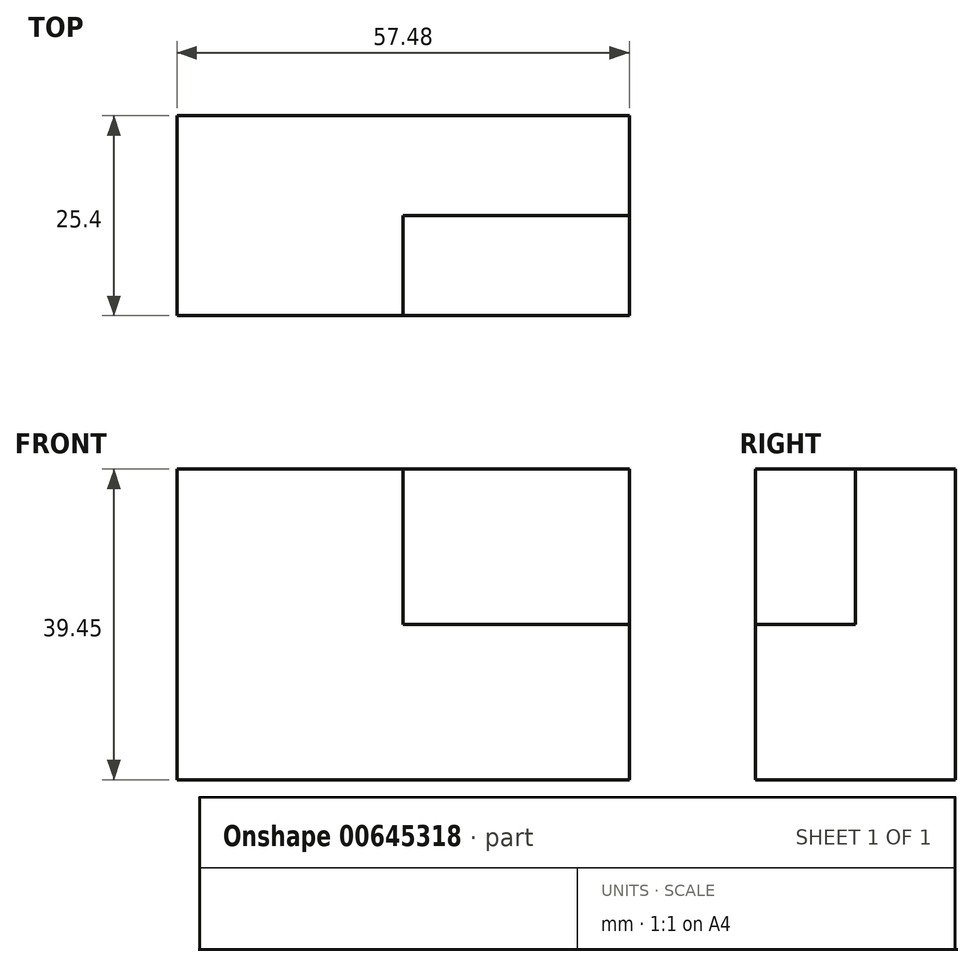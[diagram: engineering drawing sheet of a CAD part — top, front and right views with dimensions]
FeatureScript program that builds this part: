
annotation { "Feature Type Name" : "Feature", "Feature Type Description" : "" }
export const myFeature = defineFeature(function(context is Context, id is Id, definition is map)
    precondition{}
    {
        {
            var Q0;
            Q0=qCreatedBy(makeId("Front.planeOp"),FACE);
            var sketch = newSketch(context, id + "F0", { "sketchPlane" : qUnion([Q0])});
            skLineSegment(sketch, "E0.bottom", {"start": v(0, 0) * mm, "end": v(57.48, 0) * mm});
            skLineSegment(sketch, "E0.top", {"start": v(0, 39.45) * mm, "end": v(57.48, 39.45) * mm});
            skLineSegment(sketch, "E0.left", {"start": v(0, 0) * mm, "end": v(0, 39.45) * mm});
            skLineSegment(sketch, "E0.right", {"start": v(57.48, 0) * mm, "end": v(57.48, 39.45) * mm});
            skSolve(sketch);
        }
        {
            var Q0;
            Q0 = qSketchRegion(id + "F0", true);
            extrude(context, id + "F1", {"entities" : qUnion([Q0]), "depth" : 25.4 * mm, "offsetDistance" : 25.4 * mm});
        }
        {
            var Q0;
            Q0=makeQuery(id+"F1.opExtrude","CAP_FACE",FACE,{"disambiguationData":[OSD([sQuery(id+"F0.wireOp",EDGE,"E0.bottom"),sQuery(id+"F0.wireOp",EDGE,"E0.top"),sQuery(id+"F0.wireOp",EDGE,"E0.left"),sQuery(id+"F0.wireOp",EDGE,"E0.right")])],"isStart":false});
            var sketch = newSketch(context, id + "F2", { "sketchPlane" : qUnion([Q0])});
            skPoint(sketch, "E1.oppositeSnap0", {"position": v(57.48, 19.73) * mm});
            skPoint(sketch, "E1.oppositeSnap1", {"position": v(28.74, 39.45) * mm});
            skLineSegment(sketch, "E1.bottom", {"start": v(57.48, 39.45) * mm, "end": v(28.74, 39.45) * mm});
            skLineSegment(sketch, "E1.top", {"start": v(57.48, 19.73) * mm, "end": v(28.74, 19.73) * mm});
            skLineSegment(sketch, "E1.left", {"start": v(57.48, 39.45) * mm, "end": v(57.48, 19.73) * mm});
            skLineSegment(sketch, "E1.right", {"start": v(28.74, 39.45) * mm, "end": v(28.74, 19.73) * mm});
            skSolve(sketch);
        }
        {
            var Q0;
            Q0 = qSketchRegion(id + "F2", true);
            extrude(context, id + "F3", {"entities" : qUnion([Q0]), "operationType" : NewBodyOperationType.REMOVE, "oppositeDirection" : true, "depth" : 12.7 * mm, "offsetDistance" : 25.4 * mm});
        }
    });
